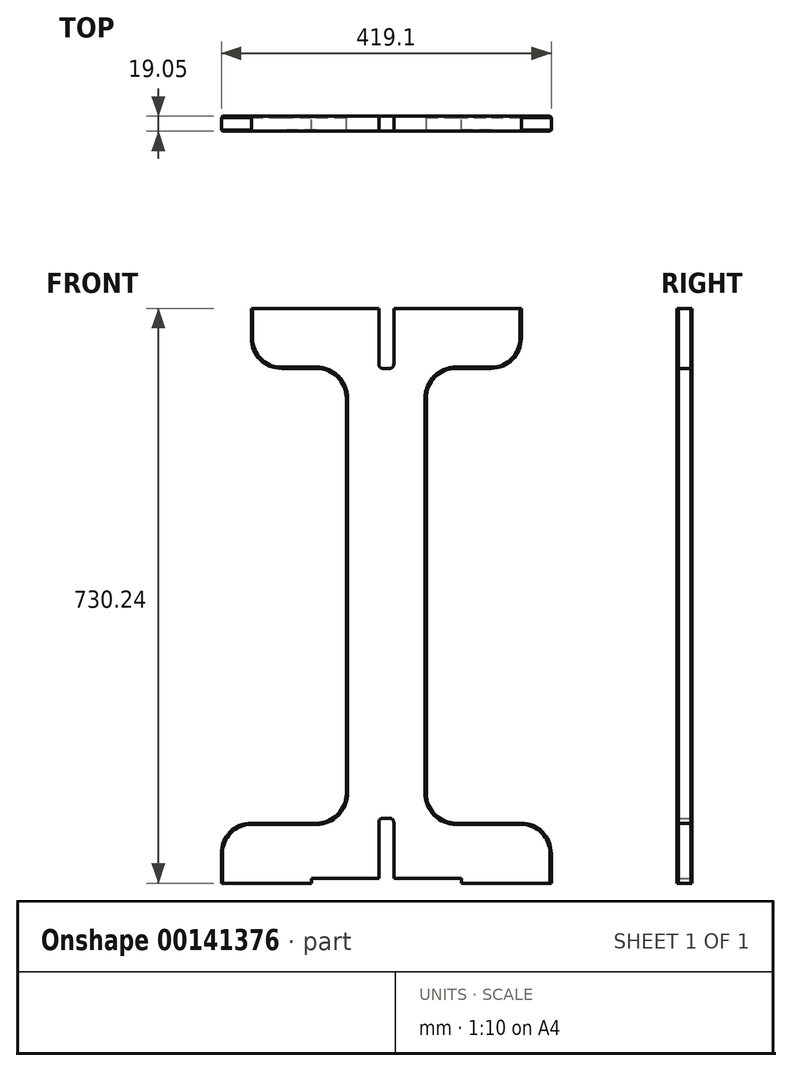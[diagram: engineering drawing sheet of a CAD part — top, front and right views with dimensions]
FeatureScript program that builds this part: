
annotation { "Feature Type Name" : "Feature", "Feature Type Description" : "" }
export const myFeature = defineFeature(function(context is Context, id is Id, definition is map)
    precondition{}
    {
        {
            var Q0;
            Q0=qCreatedBy(makeId("Front.planeOp"),FACE);
            var sketch = newSketch(context, id + "F0", { "sketchPlane" : qUnion([Q0])});
            skLineSegment(sketch, "E0.left", {"start": v(50.8, 288.93) * mm, "end": v(50.8, -288.93) * mm});
            skLineSegment(sketch, "E0.right", {"start": v(-50.8, 288.93) * mm, "end": v(-50.8, -288.93) * mm});
            skPoint(sketch, "E0.middle", {"position": v(0, 0) * mm});
            skLineSegment(sketch, "E1", {"start": v(-209.55, -365.13) * mm, "end": v(-209.55, -288.93) * mm});
            skLineSegment(sketch, "E2", {"start": v(-209.55, -288.93) * mm, "end": v(-50.8, -288.93) * mm});
            skLineSegment(sketch, "E3", {"start": v(209.55, -365.12) * mm, "end": v(209.55, -288.92) * mm});
            skLineSegment(sketch, "E4", {"start": v(209.55, -288.92) * mm, "end": v(50.8, -288.93) * mm});
            skLineSegment(sketch, "E5", {"start": v(171.45, 365.12) * mm, "end": v(171.45, 288.92) * mm});
            skLineSegment(sketch, "E6", {"start": v(171.45, 288.93) * mm, "end": v(50.8, 288.93) * mm});
            skLineSegment(sketch, "E7", {"start": v(-171.45, 365.12) * mm, "end": v(-171.45, 288.93) * mm});
            skLineSegment(sketch, "E8", {"start": v(-171.45, 288.93) * mm, "end": v(-50.8, 288.93) * mm});
            skLineSegment(sketch, "E9", {"start": v(-171.45, 365.12) * mm, "end": v(-9.53, 365.12) * mm});
            skLineSegment(sketch, "E10", {"start": v(-9.53, 365.12) * mm, "end": v(-9.53, 288.92) * mm});
            skLineSegment(sketch, "E11", {"start": v(-9.53, 288.92) * mm, "end": v(9.52, 288.92) * mm});
            skLineSegment(sketch, "E12", {"start": v(9.52, 288.92) * mm, "end": v(9.52, 365.12) * mm});
            skLineSegment(sketch, "E13", {"start": v(9.52, 365.12) * mm, "end": v(171.45, 365.12) * mm});
            skLineSegment(sketch, "E14", {"start": v(209.55, -365.12) * mm, "end": v(95.25, -365.12) * mm});
            skLineSegment(sketch, "E15", {"start": v(95.25, -365.12) * mm, "end": v(95.25, -358.78) * mm});
            skLineSegment(sketch, "E16", {"start": v(95.25, -358.77) * mm, "end": v(9.53, -358.77) * mm});
            skLineSegment(sketch, "E17", {"start": v(9.53, -358.77) * mm, "end": v(9.53, -282.57) * mm});
            skLineSegment(sketch, "E18", {"start": v(9.53, -282.57) * mm, "end": v(-9.53, -282.57) * mm});
            skLineSegment(sketch, "E19", {"start": v(-9.53, -282.57) * mm, "end": v(-9.52, -358.77) * mm});
            skLineSegment(sketch, "E20", {"start": v(-9.52, -358.77) * mm, "end": v(-95.25, -358.77) * mm});
            skLineSegment(sketch, "E21", {"start": v(-95.25, -358.77) * mm, "end": v(-95.25, -365.12) * mm});
            skLineSegment(sketch, "E22", {"start": v(-95.25, -365.12) * mm, "end": v(-209.55, -365.13) * mm});
            skSolve(sketch);
        }
        {
            var Q0;
            Q0=makeQuery(id+"F0.imprint","IMPRINT",FACE,{"disambiguationData":[TD([[makeQuery(id+"F0.imprint","IMPRINT",EDGE,{"derivedFrom":sQuery(id+"F0.wireOp",EDGE,"E0.left")}),-1.0]])]});
            extrude(context, id + "F1", {"entities" : qUnion([Q0]), "depth" : 19.05 * mm});
        }
        {
            var Q0;
            Q0=makeQuery(id+"F1.opExtrude","SWEPT_EDGE",EDGE,{"disambiguationData":[OSD([sQuery(id+"F0.wireOp",EDGE,"E0.left"),sQuery(id+"F0.wireOp",EDGE,"E6")])]});
            var Q1;
            Q1=makeQuery(id+"F1.opExtrude","SWEPT_EDGE",EDGE,{"disambiguationData":[OSD([sQuery(id+"F0.wireOp",EDGE,"E0.right"),sQuery(id+"F0.wireOp",EDGE,"E8")])]});
            var Q2;
            Q2=makeQuery(id+"F1.opExtrude","SWEPT_EDGE",EDGE,{"disambiguationData":[OSD([sQuery(id+"F0.wireOp",EDGE,"E5"),sQuery(id+"F0.wireOp",EDGE,"E6")])]});
            var Q3;
            Q3=makeQuery(id+"F1.opExtrude","SWEPT_EDGE",EDGE,{"disambiguationData":[OSD([sQuery(id+"F0.wireOp",EDGE,"E7"),sQuery(id+"F0.wireOp",EDGE,"E8")])]});
            var Q4;
            Q4=makeQuery(id+"F1.opExtrude","SWEPT_EDGE",EDGE,{"disambiguationData":[OSD([sQuery(id+"F0.wireOp",EDGE,"E1"),sQuery(id+"F0.wireOp",EDGE,"E2")])]});
            var Q5;
            Q5=makeQuery(id+"F1.opExtrude","SWEPT_EDGE",EDGE,{"disambiguationData":[OSD([sQuery(id+"F0.wireOp",EDGE,"E0.left"),sQuery(id+"F0.wireOp",EDGE,"E4")])]});
            var Q6;
            Q6=makeQuery(id+"F1.opExtrude","SWEPT_EDGE",EDGE,{"disambiguationData":[OSD([sQuery(id+"F0.wireOp",EDGE,"E3"),sQuery(id+"F0.wireOp",EDGE,"E4")])]});
            var Q7;
            Q7=makeQuery(id+"F1.opExtrude","SWEPT_EDGE",EDGE,{"disambiguationData":[OSD([sQuery(id+"F0.wireOp",EDGE,"E0.right"),sQuery(id+"F0.wireOp",EDGE,"E2")])]});
            fillet(context, id + "F2", {"entities" : qUnion([Q0, Q1, Q2, Q3, Q4, Q5, Q6, Q7]), "radius" : 38.1 * mm, "tangentPropagation" : true, "allowEdgeOverflow" : false});
        }
        {
            var Q0;
            Q0=makeQuery(id+"F1.opExtrude","SWEPT_EDGE",EDGE,{"disambiguationData":[OSD([sQuery(id+"F0.wireOp",EDGE,"E11"),sQuery(id+"F0.wireOp",EDGE,"E12")])]});
            var Q1;
            Q1=makeQuery(id+"F1.opExtrude","SWEPT_EDGE",EDGE,{"disambiguationData":[OSD([sQuery(id+"F0.wireOp",EDGE,"E10"),sQuery(id+"F0.wireOp",EDGE,"E11")])]});
            fillet(context, id + "F3", {"entities" : qUnion([Q0, Q1]), "radius" : 5.08 * mm, "tangentPropagation" : true, "allowEdgeOverflow" : false});
        }
        {
            var Q0;
            Q0=makeQuery(id+"F1.opExtrude","SWEPT_EDGE",EDGE,{"disambiguationData":[OSD([sQuery(id+"F0.wireOp",EDGE,"E17"),sQuery(id+"F0.wireOp",EDGE,"E18")])]});
            var Q1;
            Q1=makeQuery(id+"F1.opExtrude","SWEPT_EDGE",EDGE,{"disambiguationData":[OSD([sQuery(id+"F0.wireOp",EDGE,"E18"),sQuery(id+"F0.wireOp",EDGE,"E19")])]});
            fillet(context, id + "F4", {"entities" : qUnion([Q0, Q1]), "radius" : 5.08 * mm, "tangentPropagation" : true, "allowEdgeOverflow" : false});
        }
        {
            var Q0;
            Q0=makeQuery(id+"F1.opExtrude","CAP_EDGE",EDGE,{"disambiguationData":[OSD([sQuery(id+"F0.wireOp",EDGE,"E0.right")])],"isStart":false});
            var Q1;
            Q1=makeQuery(id+"F1.opExtrude","CAP_EDGE",EDGE,{"disambiguationData":[OSD([sQuery(id+"F0.wireOp",EDGE,"E0.right")])],"isStart":true});
            var Q2;
            Q2=makeQuery(id+"F1.opExtrude","CAP_EDGE",EDGE,{"disambiguationData":[OSD([sQuery(id+"F0.wireOp",EDGE,"E0.left")])],"isStart":false});
            var Q3;
            Q3=makeQuery(id+"F1.opExtrude","CAP_EDGE",EDGE,{"disambiguationData":[OSD([sQuery(id+"F0.wireOp",EDGE,"E0.left")])],"isStart":true});
            chamfer(context, id + "F5", {"entities" : qUnion([Q0, Q1, Q2, Q3]), "width" : 1.59 * mm, "tangentPropagation" : true});
        }
    });
